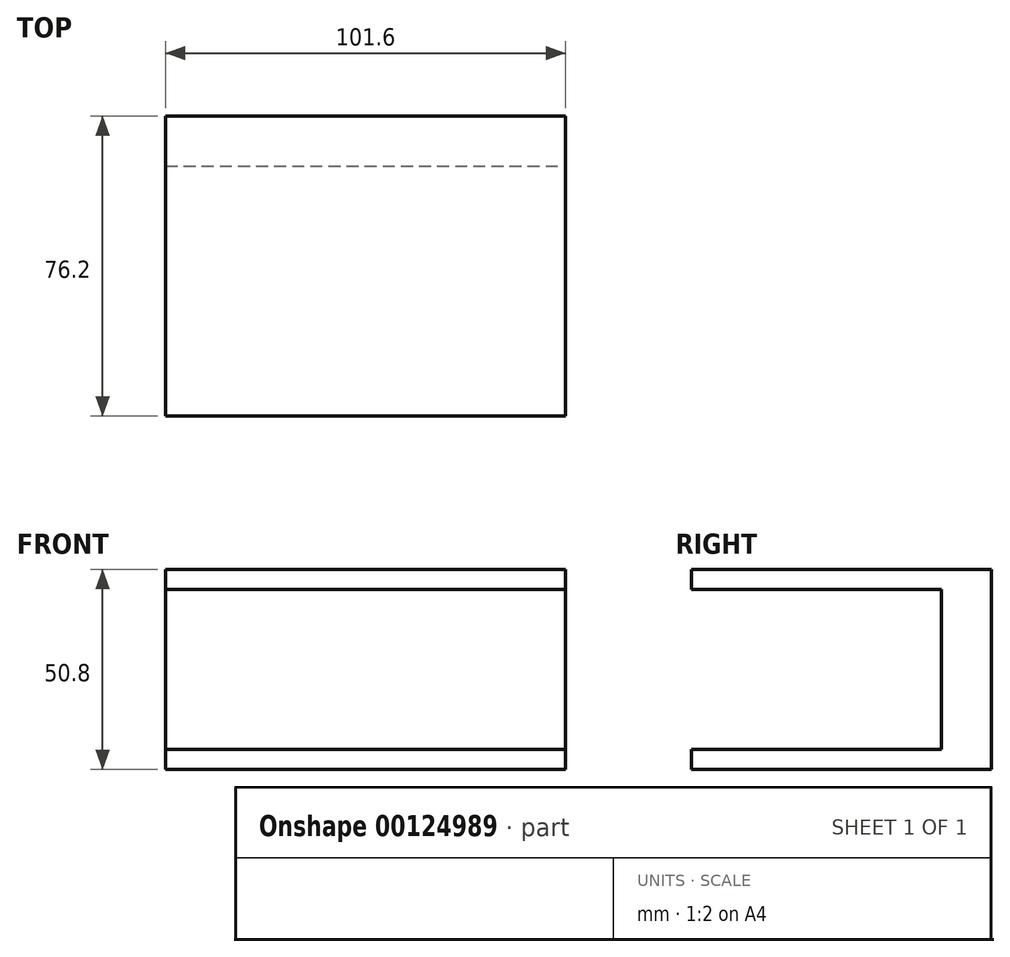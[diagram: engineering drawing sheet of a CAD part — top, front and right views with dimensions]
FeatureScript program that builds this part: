
annotation { "Feature Type Name" : "Feature", "Feature Type Description" : "" }
export const myFeature = defineFeature(function(context is Context, id is Id, definition is map)
    precondition{}
    {
        {
            var Q0;
            Q0=qCreatedBy(makeId("Front.planeOp"),FACE);
            var sketch = newSketch(context, id + "F0", { "sketchPlane" : qUnion([Q0])});
            skLineSegment(sketch, "E0.bottom", {"start": v(-50.4, 12.23) * mm, "end": v(51.2, 12.23) * mm});
            skLineSegment(sketch, "E0.top", {"start": v(-50.4, -38.57) * mm, "end": v(51.2, -38.57) * mm});
            skLineSegment(sketch, "E0.left", {"start": v(-50.4, 12.23) * mm, "end": v(-50.4, -38.57) * mm});
            skLineSegment(sketch, "E0.right", {"start": v(51.2, 12.23) * mm, "end": v(51.2, -38.57) * mm});
            skSolve(sketch);
        }
        {
            var Q0;
            Q0=makeQuery(id+"F0.imprint","IMPRINT",FACE,{"disambiguationData":[TD([[makeQuery(id+"F0.imprint","IMPRINT",EDGE,{"derivedFrom":sQuery(id+"F0.wireOp",EDGE,"E0.bottom")}),-1.0]])]});
            extrude(context, id + "F1", {"entities" : qUnion([Q0]), "oppositeDirection" : true, "depth" : 76.2 * mm});
        }
        {
            var Q0;
            Q0=makeQuery(id+"F1.opExtrude","CAP_FACE",FACE,{"disambiguationData":[OSD([sQuery(id+"F0.wireOp",EDGE,"E0.bottom"),sQuery(id+"F0.wireOp",EDGE,"E0.top"),sQuery(id+"F0.wireOp",EDGE,"E0.left"),sQuery(id+"F0.wireOp",EDGE,"E0.right")])],"isStart":true});
            var sketch = newSketch(context, id + "F2", { "sketchPlane" : qUnion([Q0])});
            skLineSegment(sketch, "E1.bottom", {"start": v(-50.4, -33.5) * mm, "end": v(51.2, -33.5) * mm});
            skLineSegment(sketch, "E1.top", {"start": v(-50.4, 7.15) * mm, "end": v(51.2, 7.15) * mm});
            skLineSegment(sketch, "E1.left", {"start": v(-50.4, -33.5) * mm, "end": v(-50.4, 7.15) * mm});
            skLineSegment(sketch, "E1.right", {"start": v(51.2, -33.5) * mm, "end": v(51.2, 7.15) * mm});
            skSolve(sketch);
        }
        {
            var Q0;
            Q0=makeQuery(id+"F2.imprint","IMPRINT",FACE,{"disambiguationData":[TD([[makeQuery(id+"F2.imprint","IMPRINT",EDGE,{"derivedFrom":sQuery(id+"F2.wireOp",EDGE,"E1.bottom")}),1.0]])]});
            var sketch = newSketch(context, id + "F3", { "sketchPlane" : qUnion([Q0])});
            skSolve(sketch);
        }
        {
            var Q0;
            Q0=makeQuery(id+"F3.imprint","IMPRINT",FACE,{"disambiguationData":[TD([[makeQuery(id+"F3.imprint","IMPRINT",EDGE,{"derivedFrom":makeQuery(id+"F2.imprint","IMPRINT",EDGE,{"derivedFrom":sQuery(id+"F2.wireOp",EDGE,"E1.bottom")})}),1.0]])]});
            extrude(context, id + "F4", {"entities" : qUnion([Q0]), "operationType" : NewBodyOperationType.REMOVE, "oppositeDirection" : true, "depth" : 63.5 * mm});
        }
        {
            var Q0;
            Q0=makeQuery(id+"F1.opExtrude","SWEPT_FACE",FACE,{"disambiguationData":[OSD([sQuery(id+"F0.wireOp",EDGE,"E0.bottom")])]});
            var sketch = newSketch(context, id + "F5", { "sketchPlane" : qUnion([Q0])});
            skCircle(sketch, "E2", {"center": v(-16.49, 41.95) * mm, "radius": 6.35 * mm});
            skCircle(sketch, "E3", {"center": v(21.27, 41.95) * mm, "radius": 6.5 * mm});
            skSolve(sketch);
        }
        {
            var Q0;
            Q0=sQuery(id+"F5.wireOp",EDGE,"E2");
            var Q1;
            Q1=sQuery(id+"F5.wireOp",EDGE,"E3");
            extrude(context, id + "F6", {"bodyType" : ToolBodyType.SURFACE, "surfaceEntities" : qUnion([Q0, Q1]), "depth" : 33.28 * mm});
        }
    });
